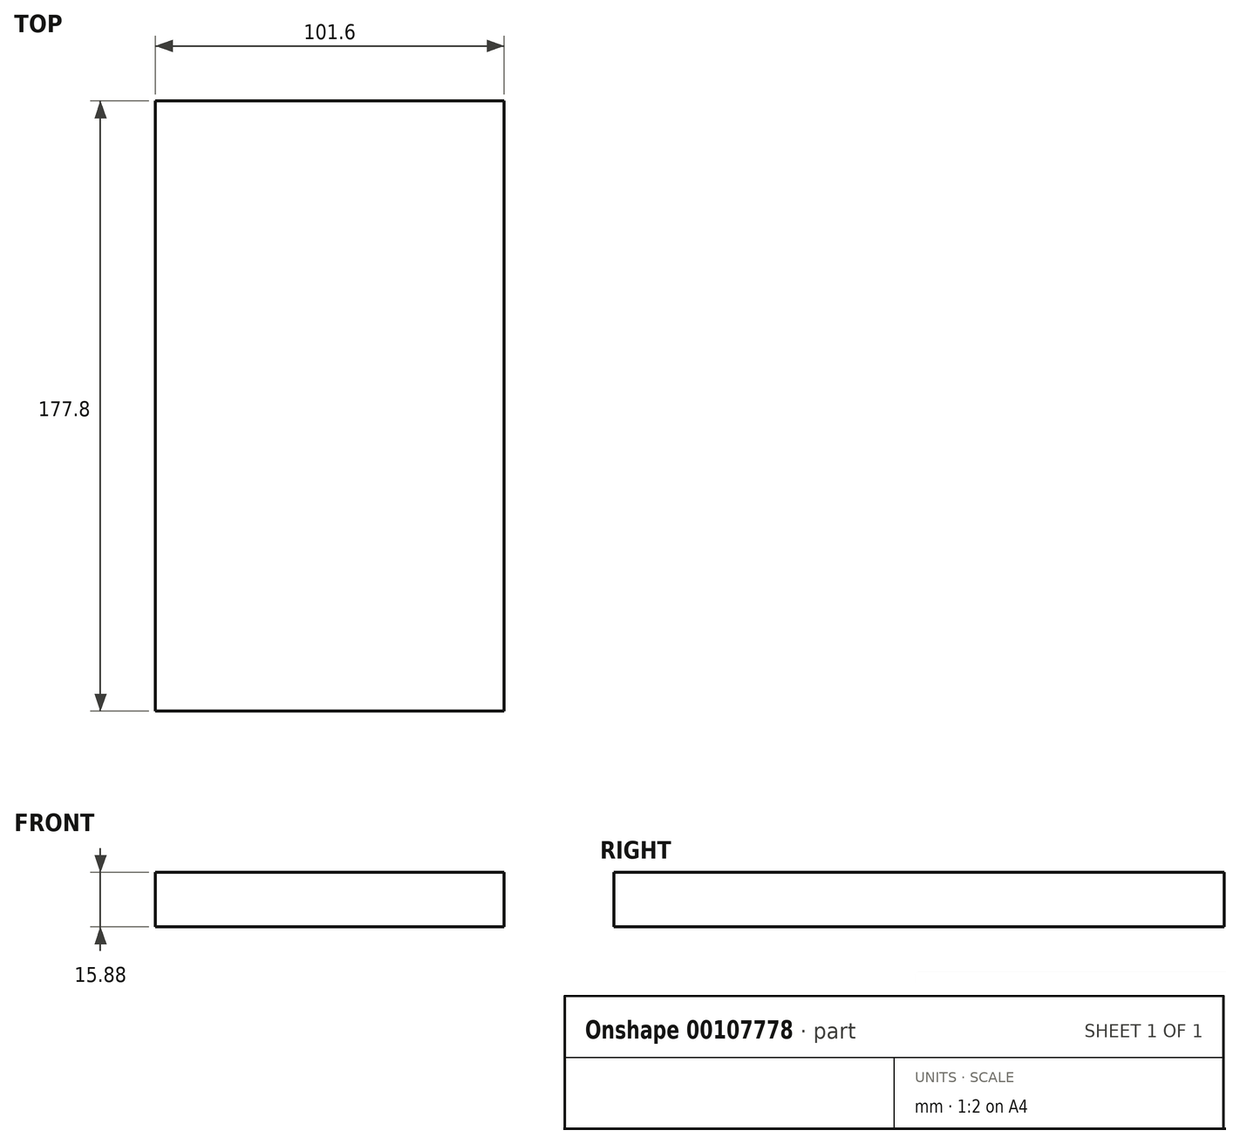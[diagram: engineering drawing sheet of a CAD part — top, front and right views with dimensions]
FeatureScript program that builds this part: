
annotation { "Feature Type Name" : "Feature", "Feature Type Description" : "" }
export const myFeature = defineFeature(function(context is Context, id is Id, definition is map)
    precondition{}
    {
        {
            var Q0;
            Q0=qCreatedBy(makeId("Top.planeOp"),FACE);
            var sketch = newSketch(context, id + "F0", { "sketchPlane" : qUnion([Q0])});
            skLineSegment(sketch, "E0.bottom", {"start": v(-74.65, 124.12) * mm, "end": v(26.95, 124.12) * mm});
            skLineSegment(sketch, "E0.top", {"start": v(-74.65, -53.68) * mm, "end": v(26.95, -53.68) * mm});
            skLineSegment(sketch, "E0.left", {"start": v(-74.65, 124.12) * mm, "end": v(-74.65, -53.68) * mm});
            skLineSegment(sketch, "E0.right", {"start": v(26.95, 124.12) * mm, "end": v(26.95, -53.68) * mm});
            skSolve(sketch);
        }
        {
            var Q0;
            Q0=makeQuery(id+"F0.imprint","IMPRINT",FACE,{"disambiguationData":[TD([[makeQuery(id+"F0.imprint","IMPRINT",EDGE,{"derivedFrom":sQuery(id+"F0.wireOp",EDGE,"E0.bottom")}),-1.0]])]});
            extrude(context, id + "F1", {"entities" : qUnion([Q0]), "depth" : 15.88 * mm});
        }
    });
